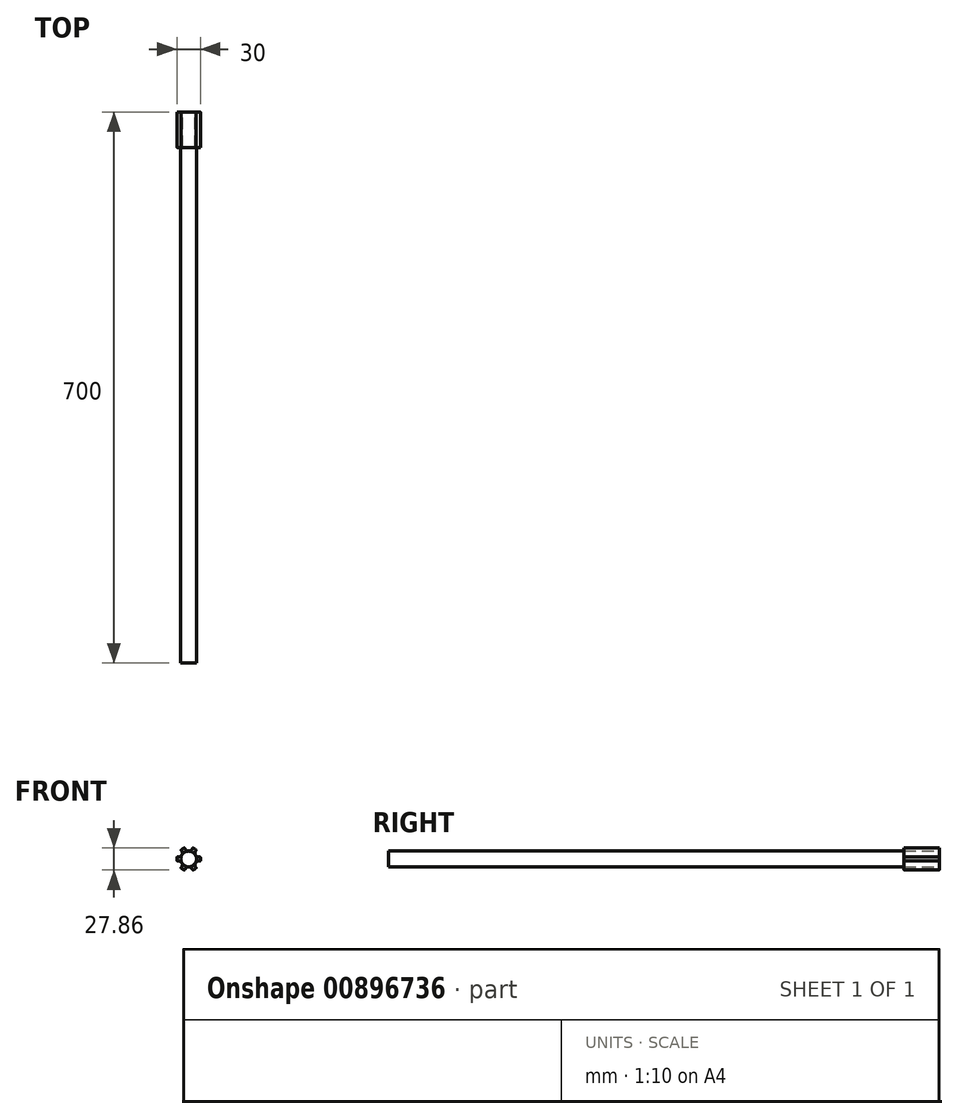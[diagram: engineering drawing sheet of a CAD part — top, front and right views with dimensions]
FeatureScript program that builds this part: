
annotation { "Feature Type Name" : "Feature", "Feature Type Description" : "" }
export const myFeature = defineFeature(function(context is Context, id is Id, definition is map)
    precondition{}
    {
        {
            var Q0;
            Q0=qCreatedBy(makeId("Front.planeOp"),FACE);
            var sketch = newSketch(context, id + "F0", { "sketchPlane" : qUnion([Q0])});
            skCircle(sketch, "E0", {"center": v(0, 0) * mm, "radius": 10 * mm});
            skArc(sketch, "E1", {"start": v(-4.93, 14.17) * mm, "mid": v(-7.5, 13) * mm, "end": v(-9.8, 11.35) * mm});
            skArc(sketch, "E2", {"start": v(-4.93, 14.17) * mm, "mid": v(0, 10) * mm, "end": v(4.93, 14.17) * mm});
            skArc(sketch, "E3.1.0", {"start": v(-14.73, 2.81) * mm, "mid": v(-8.66, 5) * mm, "end": v(-9.8, 11.35) * mm});
            skArc(sketch, "E3.2.0", {"start": v(-9.8, -11.35) * mm, "mid": v(-8.66, -5) * mm, "end": v(-14.73, -2.81) * mm});
            skArc(sketch, "E3.3.0", {"start": v(4.93, -14.17) * mm, "mid": v(0, -10) * mm, "end": v(-4.93, -14.17) * mm});
            skArc(sketch, "E3.4.0", {"start": v(14.73, -2.81) * mm, "mid": v(8.66, -5) * mm, "end": v(9.8, -11.35) * mm});
            skArc(sketch, "E3.5.0", {"start": v(9.8, 11.35) * mm, "mid": v(8.66, 5) * mm, "end": v(14.73, 2.81) * mm});
            skArc(sketch, "E4.trimOffspring", {"start": v(-14.73, 2.81) * mm, "mid": v(-15, 0) * mm, "end": v(-14.73, -2.81) * mm});
            skArc(sketch, "E5.trimOffspring", {"start": v(9.8, 11.35) * mm, "mid": v(7.5, 13) * mm, "end": v(4.93, 14.17) * mm});
            skArc(sketch, "E6.trimOffspring", {"start": v(14.73, -2.81) * mm, "mid": v(15, 0) * mm, "end": v(14.73, 2.81) * mm});
            skArc(sketch, "E7.trimOffspring", {"start": v(4.93, -14.17) * mm, "mid": v(7.5, -13) * mm, "end": v(9.8, -11.35) * mm});
            skArc(sketch, "E8.trimOffspring", {"start": v(-9.8, -11.35) * mm, "mid": v(-7.5, -13) * mm, "end": v(-4.93, -14.17) * mm});
            skSolve(sketch);
        }
        {
            var Q0;
            {var subQ0=sQuery(id+"F0.wireOp",EDGE,"E0");var subQ5=makeQuery(id+"F0.imprint","INTERSECT",VERTEX,{"derivedFrom":[sQuery(id+"F0.wireOp",EDGE,"E3.4.0"),subQ0]});Q0=makeQuery(id+"F0.imprint","IMPRINT",FACE,{"disambiguationData":[TD([[makeQuery(id+"F0.imprint","IMPRINT",EDGE,{"disambiguationData":[TD([[subQ5,-1.0]])],"derivedFrom":subQ0}),1.0]])]});}
            extrude(context, id + "F1", {"entities" : qUnion([Q0]), "depth" : 700 * mm, "offsetDistance" : 25 * mm});
        }
        {
            var Q0;
            Q0 = qSketchRegion(id + "F0", true);
            extrude(context, id + "F2", {"entities" : qUnion([Q0]), "operationType" : NewBodyOperationType.ADD, "depth" : 45 * mm, "offsetDistance" : 25 * mm});
        }
        {
            var Q0;
            Q0=makeQuery(id+"F2.opExtrude","SWEPT_EDGE",EDGE,{"disambiguationData":[OSD([sQuery(id+"F0.wireOp",EDGE,"E3.4.0"),sQuery(id+"F0.wireOp",EDGE,"E6.trimOffspring")])]});
            var Q1;
            Q1=makeQuery(id+"F2.opExtrude","SWEPT_EDGE",EDGE,{"disambiguationData":[OSD([sQuery(id+"F0.wireOp",EDGE,"E3.4.0"),sQuery(id+"F0.wireOp",EDGE,"E7.trimOffspring")])]});
            var Q2;
            Q2=makeQuery(id+"F2.opExtrude","SWEPT_EDGE",EDGE,{"disambiguationData":[OSD([sQuery(id+"F0.wireOp",EDGE,"E3.3.0"),sQuery(id+"F0.wireOp",EDGE,"E7.trimOffspring")])]});
            var Q3;
            Q3=makeQuery(id+"F2.opExtrude","SWEPT_EDGE",EDGE,{"disambiguationData":[OSD([sQuery(id+"F0.wireOp",EDGE,"E3.3.0"),sQuery(id+"F0.wireOp",EDGE,"E8.trimOffspring")])]});
            var Q4;
            Q4=makeQuery(id+"F2.opExtrude","SWEPT_EDGE",EDGE,{"disambiguationData":[OSD([sQuery(id+"F0.wireOp",EDGE,"E3.2.0"),sQuery(id+"F0.wireOp",EDGE,"E8.trimOffspring")])]});
            var Q5;
            Q5=makeQuery(id+"F2.opExtrude","SWEPT_EDGE",EDGE,{"disambiguationData":[OSD([sQuery(id+"F0.wireOp",EDGE,"E3.2.0"),sQuery(id+"F0.wireOp",EDGE,"E4.trimOffspring")])]});
            var Q6;
            Q6=makeQuery(id+"F2.opExtrude","SWEPT_EDGE",EDGE,{"disambiguationData":[OSD([sQuery(id+"F0.wireOp",EDGE,"E3.1.0"),sQuery(id+"F0.wireOp",EDGE,"E4.trimOffspring")])]});
            var Q7;
            Q7=makeQuery(id+"F2.opExtrude","SWEPT_EDGE",EDGE,{"disambiguationData":[OSD([sQuery(id+"F0.wireOp",EDGE,"E1"),sQuery(id+"F0.wireOp",EDGE,"E3.1.0")])]});
            var Q8;
            Q8=makeQuery(id+"F2.opExtrude","SWEPT_EDGE",EDGE,{"disambiguationData":[OSD([sQuery(id+"F0.wireOp",EDGE,"E1"),sQuery(id+"F0.wireOp",EDGE,"E2")])]});
            var Q9;
            Q9=makeQuery(id+"F2.opExtrude","SWEPT_EDGE",EDGE,{"disambiguationData":[OSD([sQuery(id+"F0.wireOp",EDGE,"E2"),sQuery(id+"F0.wireOp",EDGE,"E5.trimOffspring")])]});
            var Q10;
            Q10=makeQuery(id+"F2.opExtrude","SWEPT_EDGE",EDGE,{"disambiguationData":[OSD([sQuery(id+"F0.wireOp",EDGE,"E3.5.0"),sQuery(id+"F0.wireOp",EDGE,"E5.trimOffspring")])]});
            var Q11;
            Q11=makeQuery(id+"F2.opExtrude","SWEPT_EDGE",EDGE,{"disambiguationData":[OSD([sQuery(id+"F0.wireOp",EDGE,"E3.5.0"),sQuery(id+"F0.wireOp",EDGE,"E6.trimOffspring")])]});
            fillet(context, id + "F3", {"entities" : qUnion([Q0, Q1, Q2, Q3, Q4, Q5, Q6, Q7, Q8, Q9, Q10, Q11]), "radius" : 0.7 * mm, "tangentPropagation" : true, "allowEdgeOverflow" : false});
        }
    });
